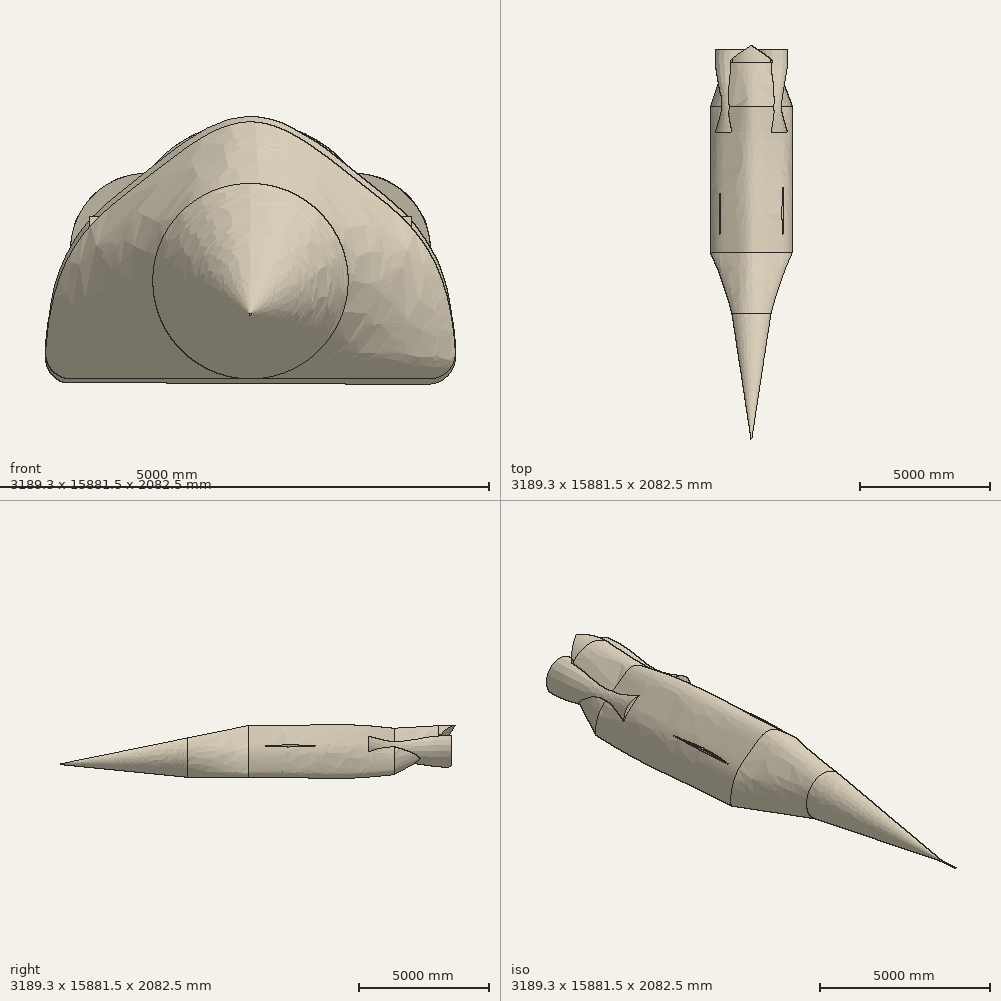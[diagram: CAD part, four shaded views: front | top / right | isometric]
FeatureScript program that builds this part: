
annotation { "Feature Type Name" : "Feature", "Feature Type Description" : "" }
export const myFeature = defineFeature(function(context is Context, id is Id, definition is map)
    precondition{}
    {
        {
            var Q0;
            Q0=qCreatedBy(makeId("Right.planeOp"),FACE);
            var sketch = newSketch(context, id + "F0", { "sketchPlane" : qUnion([Q0])});
            skLineSegment(sketch, "E0", {"start": v(0, 0) * mm, "end": v(-1750, 0) * mm});
            skLineSegment(sketch, "E1", {"start": v(-1750, 0) * mm, "end": v(-3500, 0) * mm});
            skLineSegment(sketch, "E2", {"start": v(-3500, 0) * mm, "end": v(-3500, -1000) * mm});
            skLineSegment(sketch, "E3", {"start": v(-3500, -1000) * mm, "end": v(-8500, -1000) * mm});
            skLineSegment(sketch, "E4", {"start": v(-8500, -1000) * mm, "end": v(-8500, -499.31) * mm});
            skLineSegment(sketch, "E5", {"start": v(-1151.4, 0) * mm, "end": v(-1151.4, 1000) * mm});
            skLineSegment(sketch, "E6", {"start": v(-1151.4, 1000) * mm, "end": v(-8500, -499.31) * mm});
            skLineSegment(sketch, "E7", {"start": v(-8500, -499.31) * mm, "end": v(-3500, -1000) * mm});
            skLineSegment(sketch, "E8", {"start": v(-3500, 0) * mm, "end": v(-3500, 520.82) * mm});
            skLineSegment(sketch, "E9", {"start": v(-8500, -499.31) * mm, "end": v(-8450, -499.31) * mm});
            skLineSegment(sketch, "E10", {"start": v(-8450, -499.31) * mm, "end": v(-8450, -489.1) * mm});
            skLineSegment(sketch, "E11", {"start": v(-8450, -499.31) * mm, "end": v(-8450, -504.32) * mm});
            skSolve(sketch);
        }
        {
            var Q0;
            Q0=sQuery(id+"F0.wireOp",EDGE,"E5");
            cPlane(context, id + "F1", {"entities" : qUnion([Q0]), "cplaneType" : CPlaneType.LINE_ANGLE, "offset" : 25 * mm, "angle" : 90 * degree, "oppositeDirection" : true, "width" : 150 * mm, "height" : 150 * mm});
        }
        {
            var Q0;
            Q0=qCreatedBy(id+"F1.planeOp",FACE);
            var sketch = newSketch(context, id + "F2", { "sketchPlane" : qUnion([Q0])});
            skLineSegment(sketch, "E12.top", {"start": v(-1394.2, -1000) * mm, "end": v(1394.2, -1000) * mm});
            skPoint(sketch, "E12.middle", {"position": v(0, 0) * mm});
            skFitSpline(sketch, "E13", {"points": [v(-1600, -1000) * mm, v(-848, 530) * mm, v(0, 1000) * mm, v(848, 530) * mm, v(1600, -1000) * mm], "startDerivative": vector(0, 10524.75) * mm, "endDerivative": vector(0, -10524.75) * mm});
            skArc(sketch, "E14", {"start": v(-735.27, 618.52) * mm, "mid": v(-1273.27, 435.52) * mm, "end": v(-1440.68, -107.53) * mm});
            skArc(sketch, "E15", {"start": v(1440.68, -107.53) * mm, "mid": v(1273.27, 435.52) * mm, "end": v(735.27, 618.52) * mm});
            skFitSpline(sketch, "E16.trimOffspring", {"points": [v(-1600, -1000) * mm, v(-848, 530) * mm, v(0, 1000) * mm, v(848, 530) * mm, v(1600, -1000) * mm], "startDerivative": vector(0, 10524.75) * mm, "endDerivative": vector(0, -10524.75) * mm});
            skFitSpline(sketch, "E17.trimOffspring", {"points": [v(-1600, -1000) * mm, v(-848, 530) * mm, v(0, 1000) * mm, v(848, 530) * mm, v(1600, -1000) * mm], "startDerivative": vector(0, 10524.75) * mm, "endDerivative": vector(0, -10524.75) * mm});
            skArc(sketch, "E18.filletArc", {"start": v(-1593.82, -787.83) * mm, "mid": v(-1539.85, -937.05) * mm, "end": v(-1394.2, -1000) * mm});
            skArc(sketch, "E19.filletArc", {"start": v(1394.2, -1000) * mm, "mid": v(1539.85, -937.05) * mm, "end": v(1593.82, -787.83) * mm});
            skSolve(sketch);
        }
        {
            var Q0;
            Q0=qCreatedBy(makeId("Front.planeOp"),FACE);
            var sketch = newSketch(context, id + "F3", { "sketchPlane" : qUnion([Q0])});
            skLineSegment(sketch, "E20.top", {"start": v(-1394.2, -1000) * mm, "end": v(1394.2, -1000) * mm});
            skPoint(sketch, "E20.middle", {"position": v(0, 0) * mm});
            skFitSpline(sketch, "E21", {"points": [v(-1600, -1000) * mm, v(-848, 530) * mm, v(0, 1000) * mm, v(848, 530) * mm, v(1600, -1000) * mm], "startDerivative": vector(0, 10524.75) * mm, "endDerivative": vector(0, -10524.75) * mm});
            skArc(sketch, "E22", {"start": v(-735.27, 618.52) * mm, "mid": v(-1273.27, 435.52) * mm, "end": v(-1440.68, -107.53) * mm});
            skArc(sketch, "E23", {"start": v(1440.68, -107.53) * mm, "mid": v(1273.27, 435.52) * mm, "end": v(735.27, 618.52) * mm});
            skFitSpline(sketch, "E24.trimOffspring", {"points": [v(-1600, -1000) * mm, v(-848, 530) * mm, v(0, 1000) * mm, v(848, 530) * mm, v(1600, -1000) * mm], "startDerivative": vector(0, 10524.75) * mm, "endDerivative": vector(0, -10524.75) * mm});
            skFitSpline(sketch, "E25.trimOffspring", {"points": [v(-1600, -1000) * mm, v(-848, 530) * mm, v(0, 1000) * mm, v(848, 530) * mm, v(1600, -1000) * mm], "startDerivative": vector(0, 10524.75) * mm, "endDerivative": vector(0, -10524.75) * mm});
            skArc(sketch, "E26.filletArc", {"start": v(-1593.82, -787.83) * mm, "mid": v(-1539.85, -937.05) * mm, "end": v(-1394.2, -1000) * mm});
            skArc(sketch, "E27.filletArc", {"start": v(1394.2, -1000) * mm, "mid": v(1539.85, -937.05) * mm, "end": v(1593.82, -787.83) * mm});
            skSolve(sketch);
        }
        {
            var Q0;
            Q0=qCreatedBy(makeId("Front.planeOp"),FACE);
            cPlane(context, id + "F4", {"entities" : qUnion([Q0]), "cplaneType" : CPlaneType.OFFSET, "offset" : 3500 * mm, "oppositeDirection" : true, "width" : 150 * mm, "height" : 150 * mm});
        }
        {
            var Q0;
            Q0=qCreatedBy(id+"F4.planeOp",FACE);
            var sketch = newSketch(context, id + "F5", { "sketchPlane" : qUnion([Q0])});
            skLineSegment(sketch, "E28.top", {"start": v(-1394.2, -1000) * mm, "end": v(1394.2, -1000) * mm});
            skPoint(sketch, "E28.middle", {"position": v(0, 0) * mm});
            skFitSpline(sketch, "E29", {"points": [v(-1600, -1000) * mm, v(-848, 530) * mm, v(0, 1000) * mm, v(848, 530) * mm, v(1600, -1000) * mm], "startDerivative": vector(0, 10524.75) * mm, "endDerivative": vector(0, -10524.75) * mm});
            skArc(sketch, "E30", {"start": v(-735.27, 618.52) * mm, "mid": v(-1273.27, 435.52) * mm, "end": v(-1440.68, -107.53) * mm});
            skArc(sketch, "E31", {"start": v(1440.68, -107.53) * mm, "mid": v(1273.27, 435.52) * mm, "end": v(735.27, 618.52) * mm});
            skFitSpline(sketch, "E32.trimOffspring", {"points": [v(-1600, -1000) * mm, v(-848, 530) * mm, v(0, 1000) * mm, v(848, 530) * mm, v(1600, -1000) * mm], "startDerivative": vector(0, 10524.75) * mm, "endDerivative": vector(0, -10524.75) * mm});
            skFitSpline(sketch, "E33.trimOffspring", {"points": [v(-1600, -1000) * mm, v(-848, 530) * mm, v(0, 1000) * mm, v(848, 530) * mm, v(1600, -1000) * mm], "startDerivative": vector(0, 10524.75) * mm, "endDerivative": vector(0, -10524.75) * mm});
            skArc(sketch, "E34.filletArc", {"start": v(-1593.82, -787.83) * mm, "mid": v(-1539.85, -937.05) * mm, "end": v(-1394.2, -1000) * mm});
            skArc(sketch, "E35.filletArc", {"start": v(1394.2, -1000) * mm, "mid": v(1539.85, -937.05) * mm, "end": v(1593.82, -787.83) * mm});
            skSolve(sketch);
        }
        {
            var Q0;
            Q0=qCreatedBy(makeId("Front.planeOp"),FACE);
            cPlane(context, id + "F6", {"entities" : qUnion([Q0]), "cplaneType" : CPlaneType.OFFSET, "offset" : 4500 * mm, "oppositeDirection" : true, "width" : 150 * mm, "height" : 150 * mm});
        }
        {
            var Q0;
            Q0=qCreatedBy(id+"F6.planeOp",FACE);
            var sketch = newSketch(context, id + "F7", { "sketchPlane" : qUnion([Q0])});
            skLineSegment(sketch, "E36.top", {"start": v(-1413.07, -900) * mm, "end": v(1413.07, -900) * mm});
            skPoint(sketch, "E36.middle", {"position": v(0, 0) * mm});
            skFitSpline(sketch, "E37", {"points": [v(-1600, -900) * mm, v(-784.42, 441.24) * mm, v(0, 900) * mm, v(784.42, 441.24) * mm, v(1600, -900) * mm], "startDerivative": vector(0, 9508.62) * mm, "endDerivative": vector(0, -9508.62) * mm});
            skArc(sketch, "E38", {"start": v(-719.25, 488.69) * mm, "mid": v(-1131.76, 394.84) * mm, "end": v(-1324.66, 18.33) * mm});
            skArc(sketch, "E39", {"start": v(1324.66, 18.33) * mm, "mid": v(1131.76, 394.84) * mm, "end": v(719.25, 488.69) * mm});
            skFitSpline(sketch, "E40.trimOffspring", {"points": [v(-1600, -900) * mm, v(-784.42, 441.24) * mm, v(0, 900) * mm, v(784.42, 441.24) * mm, v(1600, -900) * mm], "startDerivative": vector(0, 9508.62) * mm, "endDerivative": vector(0, -9508.62) * mm});
            skFitSpline(sketch, "E41.trimOffspring", {"points": [v(-1600, -900) * mm, v(-784.42, 441.24) * mm, v(0, 900) * mm, v(784.42, 441.24) * mm, v(1600, -900) * mm], "startDerivative": vector(0, 9508.62) * mm, "endDerivative": vector(0, -9508.62) * mm});
            skArc(sketch, "E42.filletArc", {"start": v(-1592.48, -705.43) * mm, "mid": v(-1545.4, -842.02) * mm, "end": v(-1413.07, -900) * mm});
            skArc(sketch, "E43.filletArc", {"start": v(1413.07, -900) * mm, "mid": v(1545.4, -842.02) * mm, "end": v(1592.48, -705.43) * mm});
            skLineSegment(sketch, "E44", {"start": v(-719.25, 488.69) * mm, "end": v(-1324.66, 18.33) * mm, "construction": true});
            skLineSegment(sketch, "E45", {"start": v(719.25, 488.69) * mm, "end": v(1324.66, 18.33) * mm, "construction": true});
            skSolve(sketch);
        }
        {
            var Q0;
            Q0=qCreatedBy(makeId("Front.planeOp"),FACE);
            cPlane(context, id + "F8", {"entities" : qUnion([Q0]), "cplaneType" : CPlaneType.OFFSET, "offset" : 6232.05 * mm, "oppositeDirection" : true, "width" : 150 * mm, "height" : 150 * mm});
        }
        {
            var Q0;
            Q0=qCreatedBy(id+"F8.planeOp",FACE);
            var sketch = newSketch(context, id + "F9", { "sketchPlane" : qUnion([Q0])});
            skArc(sketch, "E46", {"start": v(998.61, 52.63) * mm, "mid": v(0, 1000) * mm, "end": v(-998.61, 52.63) * mm});
            skLineSegment(sketch, "E47", {"start": v(0, 0) * mm, "end": v(-948.68, 0) * mm});
            skLineSegment(sketch, "E48", {"start": v(0, 0) * mm, "end": v(948.68, 0) * mm});
            skLineSegment(sketch, "E49", {"start": v(0, 1000) * mm, "end": v(0, 675) * mm, "construction": true});
            skLineSegment(sketch, "E50", {"start": v(0, 675) * mm, "end": v(-737.82, 675) * mm, "construction": true});
            skLineSegment(sketch, "E51", {"start": v(0, 675) * mm, "end": v(737.82, 675) * mm, "construction": true});
            skPoint(sketch, "E52.visualSharp", {"position": v(-1000, 0) * mm});
            skArc(sketch, "E52.filletArc", {"start": v(-998.61, 52.63) * mm, "mid": v(-984.96, 15.59) * mm, "end": v(-948.68, 0) * mm});
            skPoint(sketch, "E53.visualSharp", {"position": v(1000, 0) * mm});
            skArc(sketch, "E53.filletArc", {"start": v(948.68, 0) * mm, "mid": v(984.96, 15.59) * mm, "end": v(998.61, 52.63) * mm});
            skSolve(sketch);
        }
        {
            var Q0;
            Q0=makeQuery(id+"F2.imprint","IMPRINT",FACE,{"disambiguationData":[TD([[makeQuery(id+"F2.imprint","IMPRINT",EDGE,{"derivedFrom":sQuery(id+"F2.wireOp",EDGE,"E12.top")}),1.0]])]});
            var Q1;
            Q1=makeQuery(id+"F3.imprint","IMPRINT",FACE,{"disambiguationData":[TD([[makeQuery(id+"F3.imprint","IMPRINT",EDGE,{"derivedFrom":sQuery(id+"F3.wireOp",EDGE,"E20.top")}),1.0]])]});
            var Q2;
            Q2=makeQuery(id+"F5.imprint","IMPRINT",FACE,{"disambiguationData":[TD([[makeQuery(id+"F5.imprint","IMPRINT",EDGE,{"derivedFrom":sQuery(id+"F5.wireOp",EDGE,"E28.top")}),1.0]])]});
            var Q3;
            Q3=makeQuery(id+"F7.imprint","IMPRINT",FACE,{"disambiguationData":[TD([[makeQuery(id+"F7.imprint","IMPRINT",EDGE,{"derivedFrom":sQuery(id+"F7.wireOp",EDGE,"E36.top")}),1.0]])]});
            loft(context, id + "F10", {"sheetProfilesArray" : [{ "sheetProfileEntities" : qUnion([Q0]) }, { "sheetProfileEntities" : qUnion([Q1]) }, { "sheetProfileEntities" : qUnion([Q2]) }, { "sheetProfileEntities" : qUnion([Q3]) }]});
        }
        {
            var Q0;
            Q0=sQuery(id+"F7.wireOp",EDGE,"E44");
            var Q1;
            Q1=sQuery(id+"F9.wireOp",VERTEX,"E50.end");
            cPlane(context, id + "F11", {"entities" : qUnion([Q0, Q1]), "cplaneType" : CPlaneType.LINE_ANGLE, "offset" : 25 * mm, "angle" : 180 * degree, "width" : 150 * mm, "height" : 150 * mm});
        }
        {
            var Q0;
            Q0=qCreatedBy(id+"F11.planeOp",FACE);
            var sketch = newSketch(context, id + "F12", { "sketchPlane" : qUnion([Q0])});
            skLineSegment(sketch, "E54", {"start": v(-589.34, 4526.34) * mm, "end": v(-612.8, 6268.32) * mm});
            skLineSegment(sketch, "E55", {"start": v(-1354.08, 4472.19) * mm, "end": v(-612.8, 6268.32) * mm});
            skSolve(sketch);
        }
        {
            var Q0;
            Q0=sQuery(id+"F7.wireOp",EDGE,"E45");
            var Q1;
            Q1=sQuery(id+"F9.wireOp",VERTEX,"E51.end");
            cPlane(context, id + "F13", {"entities" : qUnion([Q0, Q1]), "cplaneType" : CPlaneType.LINE_ANGLE, "offset" : 25 * mm, "angle" : 0 * degree, "width" : 150 * mm, "height" : 150 * mm});
        }
        {
            var Q0;
            Q0=qCreatedBy(id+"F13.planeOp",FACE);
            var sketch = newSketch(context, id + "F14", { "sketchPlane" : qUnion([Q0])});
            skLineSegment(sketch, "E56", {"start": v(589.34, 4526.34) * mm, "end": v(612.8, 6268.32) * mm});
            skLineSegment(sketch, "E57", {"start": v(1354.08, 4472.19) * mm, "end": v(612.8, 6268.32) * mm});
            skSolve(sketch);
        }
        {
            var Q1;
            Q1=makeQuery(id+"F10.opLoft","CAP_FACE",FACE,{"disambiguationData":[OSD([makeQuery(id+"F7.imprint","IMPRINT",FACE,{"disambiguationData":[TD([[makeQuery(id+"F7.imprint","IMPRINT",EDGE,{"derivedFrom":sQuery(id+"F7.wireOp",EDGE,"E36.top")}),1.0]])]})])],"isStart":true});
            var Q2;
            Q2=makeQuery(id+"F9.imprint","IMPRINT",FACE,{"disambiguationData":[TD([[makeQuery(id+"F9.imprint","IMPRINT",EDGE,{"derivedFrom":sQuery(id+"F9.wireOp",EDGE,"E46")}),1.0]])]});
            var Q3;
            Q3=sQuery(id+"F12.wireOp",EDGE,"E54");
            var Q4;
            Q4=sQuery(id+"F14.wireOp",EDGE,"E56");
            loft(context, id + "F15", {"operationType" : NewBodyOperationType.ADD, "addGuides" : true, "sheetProfilesArray" : [{ "sheetProfileEntities" : qUnion([Q1]) }, { "sheetProfileEntities" : qUnion([Q2]) }], "guidesArray" : [{ "guideEntities" : qUnion([Q3]), "guideDerivativeType" : LoftGuideDerivativeType.DEFAULT, "guideDerivativeMagnitude" : 1 }, { "guideEntities" : qUnion([Q4]), "guideDerivativeType" : LoftGuideDerivativeType.DEFAULT, "guideDerivativeMagnitude" : 1 }]});
        }
        {
            var Q0;
            Q0=makeQuery(id+"F15.opLoft","CAP_FACE",FACE,{"disambiguationData":[OSD([makeQuery(id+"F9.imprint","IMPRINT",FACE,{"disambiguationData":[TD([[makeQuery(id+"F9.imprint","IMPRINT",EDGE,{"derivedFrom":sQuery(id+"F9.wireOp",EDGE,"E46")}),1.0]])]})])],"isStart":true});
            extrude(context, id + "F16", {"entities" : qUnion([Q0]), "operationType" : NewBodyOperationType.ADD, "depth" : 649.4 * mm, "offsetDistance" : 25 * mm});
        }
        {
            var Q0;
            Q0=qCreatedBy(makeId("Right.planeOp"),FACE);
            var sketch = newSketch(context, id + "F17", { "sketchPlane" : qUnion([Q0])});
            skLineSegment(sketch, "E58", {"start": v(0, 0) * mm, "end": v(4500, 0) * mm});
            skLineSegment(sketch, "E59", {"start": v(4500, 0) * mm, "end": v(6232.05, 0) * mm});
            skLineSegment(sketch, "E60", {"start": v(4500, 0) * mm, "end": v(4500, 1000) * mm});
            skLineSegment(sketch, "E61", {"start": v(4500, 1000) * mm, "end": v(6881.46, 1000) * mm});
            skLineSegment(sketch, "E62", {"start": v(6881.46, 1000) * mm, "end": v(6881.46, -1000) * mm});
            skLineSegment(sketch, "E63", {"start": v(6881.46, 1000) * mm, "end": v(6232.05, 0) * mm});
            skLineSegment(sketch, "E64", {"start": v(6232.05, 0) * mm, "end": v(5582.64, -1000) * mm});
            skLineSegment(sketch, "E65", {"start": v(5582.64, -1000) * mm, "end": v(6881.46, -1000) * mm});
            skSolve(sketch);
        }
        {
            var Q0;
            Q0=makeQuery(id+"F17.imprint","IMPRINT",FACE,{"disambiguationData":[TD([[makeQuery(id+"F17.imprint","IMPRINT",EDGE,{"derivedFrom":sQuery(id+"F17.wireOp",EDGE,"E62")}),-1.0]])]});
            var Q1;
            Q1=sQuery(id+"F17.wireOp",EDGE,"E61");
            revolve(context, id + "F18", {"operationType" : NewBodyOperationType.REMOVE, "entities" : qUnion([Q0]), "axis" : qUnion([Q1]), "revolveType" : RevolveType.SYMMETRIC, "oppositeDirection" : true, "angle" : 182 * degree});
        }
        {
            var Q0;
            Q0=qCreatedBy(id+"F1.planeOp",FACE);
            var sketch = newSketch(context, id + "F19", { "sketchPlane" : qUnion([Q0])});
            skLineSegment(sketch, "E66.top", {"start": v(-1394.2, -1000) * mm, "end": v(1394.2, -1000) * mm});
            skPoint(sketch, "E66.middle", {"position": v(0, 0) * mm});
            skFitSpline(sketch, "E67", {"points": [v(-1600, -1000) * mm, v(-848, 530) * mm, v(0, 1000) * mm, v(848, 530) * mm, v(1600, -1000) * mm], "startDerivative": vector(0, 10524.75) * mm, "endDerivative": vector(0, -10524.75) * mm});
            skArc(sketch, "E68.filletArc", {"start": v(-1593.82, -787.83) * mm, "mid": v(-1539.85, -937.05) * mm, "end": v(-1394.2, -1000) * mm});
            skArc(sketch, "E69.filletArc", {"start": v(1394.2, -1000) * mm, "mid": v(1539.85, -937.05) * mm, "end": v(1593.82, -787.83) * mm});
            skLineSegment(sketch, "E70", {"start": v(-1593.82, -787.83) * mm, "end": v(-1394.2, -1000) * mm, "construction": true});
            skLineSegment(sketch, "E71", {"start": v(1593.82, -787.83) * mm, "end": v(1394.2, -1000) * mm, "construction": true});
            skSolve(sketch);
        }
        {
            var Q0;
            Q0=qCreatedBy(makeId("Front.planeOp"),FACE);
            cPlane(context, id + "F20", {"entities" : qUnion([Q0]), "cplaneType" : CPlaneType.OFFSET, "offset" : 3500 * mm, "width" : 150 * mm, "height" : 150 * mm});
        }
        {
            var Q0;
            Q0=qCreatedBy(id+"F20.planeOp",FACE);
            var sketch = newSketch(context, id + "F21", { "sketchPlane" : qUnion([Q0])});
            skCircle(sketch, "E72", {"center": v(0, -239.59) * mm, "radius": 760.41 * mm});
            skLineSegment(sketch, "E73", {"start": v(0, -1000) * mm, "end": v(0, -800) * mm, "construction": true});
            skLineSegment(sketch, "E74", {"start": v(0, -800) * mm, "end": v(-513.97, -800) * mm, "construction": true});
            skLineSegment(sketch, "E75", {"start": v(0, -800) * mm, "end": v(513.97, -800) * mm, "construction": true});
            skSolve(sketch);
        }
        {
            var Q0;
            Q0=qCreatedBy(makeId("Front.planeOp"),FACE);
            cPlane(context, id + "F22", {"entities" : qUnion([Q0]), "cplaneType" : CPlaneType.OFFSET, "offset" : 8450 * mm, "width" : 150 * mm, "height" : 150 * mm});
        }
        {
            var Q0;
            Q0=qCreatedBy(id+"F22.planeOp",FACE);
            var sketch = newSketch(context, id + "F23", { "sketchPlane" : qUnion([Q0])});
            skCircle(sketch, "E76", {"center": v(0, -496.71) * mm, "radius": 7.6 * mm});
            skSolve(sketch);
        }
        {
            var Q0;
            Q0=sQuery(id+"F19.wireOp",EDGE,"E70");
            var Q1;
            Q1=sQuery(id+"F21.wireOp",VERTEX,"E74.end");
            cPlane(context, id + "F24", {"entities" : qUnion([Q0, Q1]), "cplaneType" : CPlaneType.LINE_ANGLE, "offset" : 25 * mm, "angle" : 0 * degree, "width" : 150 * mm, "height" : 150 * mm});
        }
        {
            var Q0;
            Q0=qCreatedBy(id+"F24.planeOp",FACE);
            var sketch = newSketch(context, id + "F25", { "sketchPlane" : qUnion([Q0])});
            skLineSegment(sketch, "E77", {"start": v(3032.27, -230.44) * mm, "end": v(558.11, 518.4) * mm});
            skLineSegment(sketch, "E78", {"start": v(3032.27, -230.44) * mm, "end": v(558.11, 227.09) * mm});
            skSolve(sketch);
        }
        {
            var Q0;
            Q0=sQuery(id+"F19.wireOp",EDGE,"E71");
            var Q1;
            Q1=sQuery(id+"F21.wireOp",VERTEX,"E75.end");
            cPlane(context, id + "F26", {"entities" : qUnion([Q0, Q1]), "cplaneType" : CPlaneType.LINE_ANGLE, "offset" : 25 * mm, "angle" : 180 * degree, "width" : 150 * mm, "height" : 150 * mm});
        }
        {
            var Q0;
            Q0=qCreatedBy(id+"F26.planeOp",FACE);
            var sketch = newSketch(context, id + "F27", { "sketchPlane" : qUnion([Q0])});
            skLineSegment(sketch, "E79", {"start": v(-3032.27, -230.44) * mm, "end": v(-558.11, 518.4) * mm});
            skLineSegment(sketch, "E80", {"start": v(-3032.27, -230.44) * mm, "end": v(-558.11, 227.09) * mm});
            skSolve(sketch);
        }
        {
            var Q1;
            Q1=makeQuery(id+"F19.imprint","IMPRINT",FACE,{"disambiguationData":[TD([[makeQuery(id+"F19.imprint","IMPRINT",EDGE,{"derivedFrom":sQuery(id+"F19.wireOp",EDGE,"E66.top")}),1.0]])]});
            var Q2;
            Q2=makeQuery(id+"F21.imprint","IMPRINT",FACE,{"disambiguationData":[TD([[makeQuery(id+"F21.imprint","IMPRINT",EDGE,{"derivedFrom":sQuery(id+"F21.wireOp",EDGE,"E72")}),1.0]])]});
            var Q3;
            Q3=sQuery(id+"F25.wireOp",EDGE,"E77");
            var Q4;
            Q4=sQuery(id+"F27.wireOp",EDGE,"E79");
            loft(context, id + "F28", {"operationType" : NewBodyOperationType.ADD, "addGuides" : true, "sheetProfilesArray" : [{ "sheetProfileEntities" : qUnion([Q1]) }, { "sheetProfileEntities" : qUnion([Q2]) }], "guidesArray" : [{ "guideEntities" : qUnion([Q3]), "guideDerivativeType" : LoftGuideDerivativeType.DEFAULT, "guideDerivativeMagnitude" : 1 }, { "guideEntities" : qUnion([Q4]), "guideDerivativeType" : LoftGuideDerivativeType.DEFAULT, "guideDerivativeMagnitude" : 1 }]});
        }
        {
            var Q1;
            Q1=makeQuery(id+"F28.opLoft","CAP_FACE",FACE,{"disambiguationData":[OSD([makeQuery(id+"F21.imprint","IMPRINT",FACE,{"disambiguationData":[TD([[makeQuery(id+"F21.imprint","IMPRINT",EDGE,{"derivedFrom":sQuery(id+"F21.wireOp",EDGE,"E72")}),1.0]])]})])],"isStart":true});
            var Q2;
            Q2=makeQuery(id+"F23.imprint","IMPRINT",FACE,{"disambiguationData":[TD([[makeQuery(id+"F23.imprint","IMPRINT",EDGE,{"derivedFrom":sQuery(id+"F23.wireOp",EDGE,"E76")}),1.0]])]});
            loft(context, id + "F29", {"operationType" : NewBodyOperationType.ADD, "sheetProfilesArray" : [{ "sheetProfileEntities" : qUnion([Q1]) }, { "sheetProfileEntities" : qUnion([Q2]) }]});
        }
        {
            var Q0;
            Q0=makeQuery(id+"F29.opLoft","CAP_FACE",FACE,{"disambiguationData":[OSD([makeQuery(id+"F23.imprint","IMPRINT",FACE,{"disambiguationData":[TD([[makeQuery(id+"F23.imprint","IMPRINT",EDGE,{"derivedFrom":sQuery(id+"F23.wireOp",EDGE,"E76")}),1.0]])]})])],"isStart":true});
            extrude(context, id + "F30", {"entities" : qUnion([Q0]), "operationType" : NewBodyOperationType.ADD, "depth" : 550 * mm, "offsetDistance" : 25 * mm});
        }
        {
            var Q0;
            Q0=qCreatedBy(makeId("Front.planeOp"),FACE);
            cPlane(context, id + "F31", {"entities" : qUnion([Q0]), "cplaneType" : CPlaneType.OFFSET, "offset" : 3500 * mm, "oppositeDirection" : true, "width" : 150 * mm, "height" : 150 * mm});
        }
        {
            var Q0;
            Q0=qCreatedBy(id+"F31.planeOp",FACE);
            var sketch = newSketch(context, id + "F32", { "sketchPlane" : qUnion([Q0])});
            skCircle(sketch, "E81", {"center": v(-800, 0) * mm, "radius": 600 * mm});
            skCircle(sketch, "E82", {"center": v(800, 0) * mm, "radius": 600 * mm});
            skSolve(sketch);
        }
        {
            var Q0;
            Q0=qCreatedBy(makeId("Front.planeOp"),FACE);
            cPlane(context, id + "F33", {"entities" : qUnion([Q0]), "cplaneType" : CPlaneType.OFFSET, "offset" : 4500 * mm, "oppositeDirection" : true, "width" : 150 * mm, "height" : 150 * mm});
        }
        {
            var Q0;
            Q0=qCreatedBy(id+"F33.planeOp",FACE);
            var sketch = newSketch(context, id + "F34", { "sketchPlane" : qUnion([Q0])});
            skCircle(sketch, "E83", {"center": v(-800, 0) * mm, "radius": 400 * mm});
            skCircle(sketch, "E84", {"center": v(800, 0) * mm, "radius": 400 * mm});
            skSolve(sketch);
        }
        {
            var Q0;
            Q0=qCreatedBy(makeId("Front.planeOp"),FACE);
            cPlane(context, id + "F35", {"entities" : qUnion([Q0]), "cplaneType" : CPlaneType.OFFSET, "offset" : 6232.05 * mm, "oppositeDirection" : true, "width" : 150 * mm, "height" : 150 * mm});
        }
        {
            var Q0;
            Q0=qCreatedBy(id+"F35.planeOp",FACE);
            var sketch = newSketch(context, id + "F36", { "sketchPlane" : qUnion([Q0])});
            skCircle(sketch, "E85", {"center": v(-800, 0) * mm, "radius": 600 * mm});
            skCircle(sketch, "E86", {"center": v(800, 0) * mm, "radius": 600 * mm});
            skSolve(sketch);
        }
        {
            var Q0;
            Q0=qCreatedBy(makeId("Front.planeOp"),FACE);
            cPlane(context, id + "F37", {"entities" : qUnion([Q0]), "cplaneType" : CPlaneType.OFFSET, "offset" : 6732.05 * mm, "oppositeDirection" : true, "width" : 150 * mm, "height" : 150 * mm});
        }
        {
            var Q0;
            Q0=qCreatedBy(id+"F37.planeOp",FACE);
            var sketch = newSketch(context, id + "F38", { "sketchPlane" : qUnion([Q0])});
            skCircle(sketch, "E87", {"center": v(-800, 0) * mm, "radius": 600 * mm});
            skCircle(sketch, "E88", {"center": v(800, 0) * mm, "radius": 600 * mm});
            skSolve(sketch);
        }
        {
            var Q0;
            Q0=makeQuery(id+"F32.imprint","IMPRINT",FACE,{"disambiguationData":[TD([[makeQuery(id+"F32.imprint","IMPRINT",EDGE,{"derivedFrom":sQuery(id+"F32.wireOp",EDGE,"E81")}),1.0]])]});
            var Q1;
            Q1=makeQuery(id+"F34.imprint","IMPRINT",FACE,{"disambiguationData":[TD([[makeQuery(id+"F34.imprint","IMPRINT",EDGE,{"derivedFrom":sQuery(id+"F34.wireOp",EDGE,"E83")}),1.0]])]});
            var Q2;
            Q2=makeQuery(id+"F36.imprint","IMPRINT",FACE,{"disambiguationData":[TD([[makeQuery(id+"F36.imprint","IMPRINT",EDGE,{"derivedFrom":sQuery(id+"F36.wireOp",EDGE,"E85")}),1.0]])]});
            var Q3;
            Q3=makeQuery(id+"F38.imprint","IMPRINT",FACE,{"disambiguationData":[TD([[makeQuery(id+"F38.imprint","IMPRINT",EDGE,{"derivedFrom":sQuery(id+"F38.wireOp",EDGE,"E87")}),1.0]])]});
            loft(context, id + "F39", {"sheetProfilesArray" : [{ "sheetProfileEntities" : qUnion([Q0]) }, { "sheetProfileEntities" : qUnion([Q1]) }, { "sheetProfileEntities" : qUnion([Q2]) }, { "sheetProfileEntities" : qUnion([Q3]) }]});
        }
        {
            var Q0;
            Q0=makeQuery(id+"F32.imprint","IMPRINT",FACE,{"disambiguationData":[TD([[makeQuery(id+"F32.imprint","IMPRINT",EDGE,{"derivedFrom":sQuery(id+"F32.wireOp",EDGE,"E82")}),1.0]])]});
            var Q1;
            Q1=makeQuery(id+"F34.imprint","IMPRINT",FACE,{"disambiguationData":[TD([[makeQuery(id+"F34.imprint","IMPRINT",EDGE,{"derivedFrom":sQuery(id+"F34.wireOp",EDGE,"E84")}),1.0]])]});
            var Q2;
            Q2=makeQuery(id+"F36.imprint","IMPRINT",FACE,{"disambiguationData":[TD([[makeQuery(id+"F36.imprint","IMPRINT",EDGE,{"derivedFrom":sQuery(id+"F36.wireOp",EDGE,"E86")}),1.0]])]});
            var Q3;
            Q3=makeQuery(id+"F38.imprint","IMPRINT",FACE,{"disambiguationData":[TD([[makeQuery(id+"F38.imprint","IMPRINT",EDGE,{"derivedFrom":sQuery(id+"F38.wireOp",EDGE,"E88")}),1.0]])]});
            loft(context, id + "F40", {"sheetProfilesArray" : [{ "sheetProfileEntities" : qUnion([Q0]) }, { "sheetProfileEntities" : qUnion([Q1]) }, { "sheetProfileEntities" : qUnion([Q2]) }, { "sheetProfileEntities" : qUnion([Q3]) }]});
        }
        {
            var Q0;
            Q0=qCreatedBy(makeId("Right.planeOp"),FACE);
            var sketch = newSketch(context, id + "F41", { "sketchPlane" : qUnion([Q0])});
            skFitSpline(sketch, "E89", {"points": [v(-1500, -50) * mm, v(0, 250) * mm, v(3000, 0) * mm, v(0, -250) * mm, v(-1500, -50) * mm]});
            skSolve(sketch);
        }
        {
            var Q0;
            Q0 = qSketchRegion(id + "F41", true);
            extrude(context, id + "F42", {"entities" : qUnion([Q0]), "endBound" : BoundingType.SYMMETRIC, "depth" : 2500 * mm, "offsetDistance" : 25 * mm});
        }
    });
